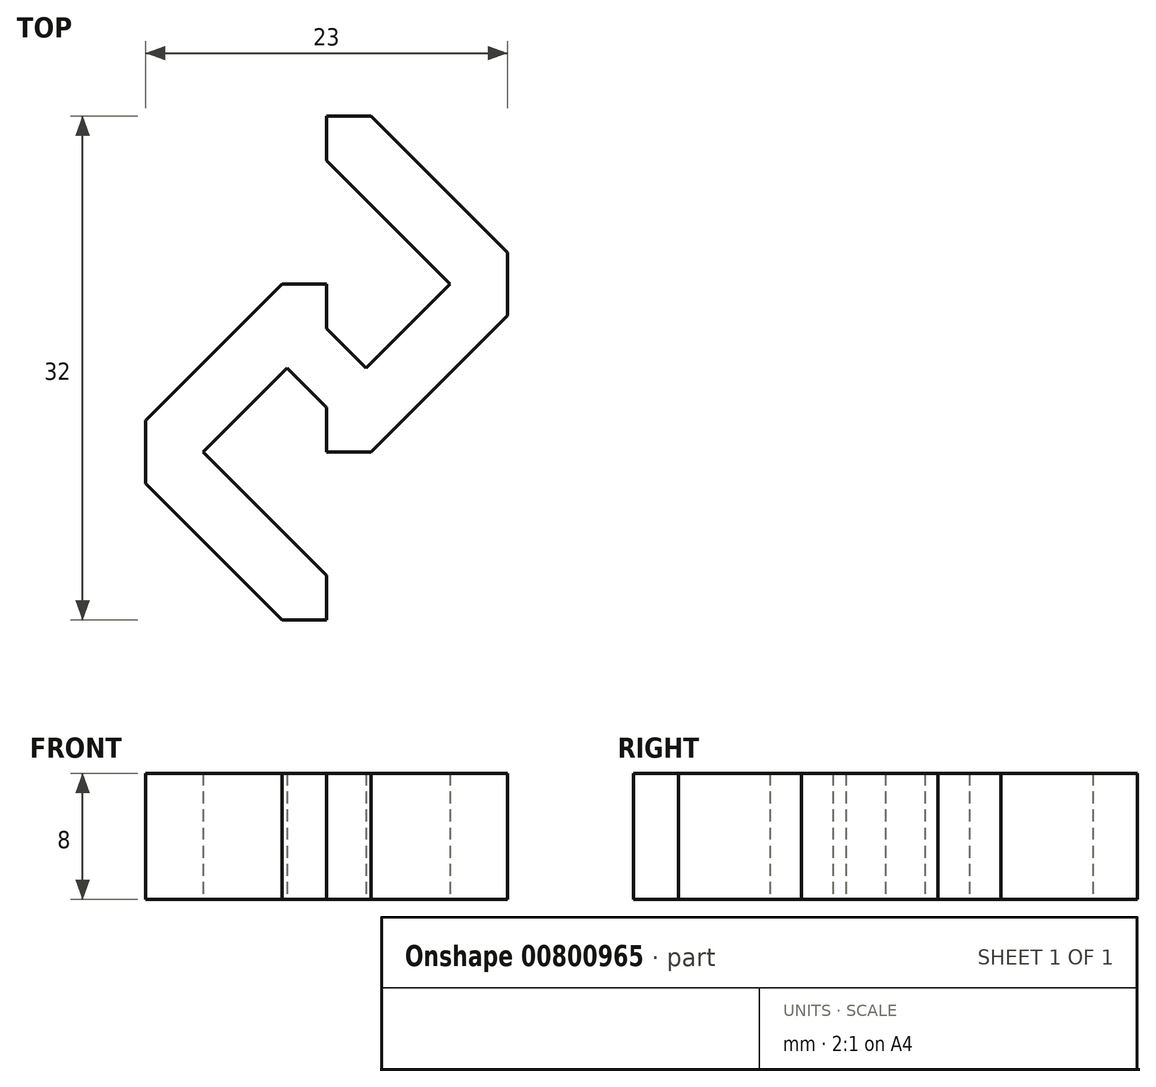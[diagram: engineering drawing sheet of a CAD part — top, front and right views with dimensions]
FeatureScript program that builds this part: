
annotation { "Feature Type Name" : "Feature", "Feature Type Description" : "" }
export const myFeature = defineFeature(function(context is Context, id is Id, definition is map)
    precondition{}
    {
        {
            var Q0;
            Q0=qCreatedBy(makeId("Top.planeOp"),FACE);
            var sketch = newSketch(context, id + "F0", { "sketchPlane" : qUnion([Q0])});
            skLineSegment(sketch, "E0", {"start": v(0, 0) * mm, "end": v(0, -2.83) * mm});
            skLineSegment(sketch, "E1", {"start": v(0, -2.83) * mm, "end": v(7.84, -10.67) * mm});
            skLineSegment(sketch, "E2", {"start": v(7.84, -10.67) * mm, "end": v(0, -18.5) * mm});
            skLineSegment(sketch, "E3", {"start": v(0, 0) * mm, "end": v(2.83, 0) * mm});
            skLineSegment(sketch, "E4", {"start": v(2.83, 0) * mm, "end": v(11.5, -8.67) * mm});
            skLineSegment(sketch, "E5", {"start": v(11.5, -8.67) * mm, "end": v(11.5, -12.67) * mm});
            skLineSegment(sketch, "E6", {"start": v(11.5, -12.67) * mm, "end": v(2.83, -21.33) * mm});
            skLineSegment(sketch, "E7", {"start": v(2.83, -21.33) * mm, "end": v(0, -21.33) * mm});
            skLineSegment(sketch, "E8", {"start": v(0, -21.33) * mm, "end": v(0, -18.5) * mm});
            skLineSegment(sketch, "E9", {"start": v(0, -13.5) * mm, "end": v(0, -10.67) * mm});
            skLineSegment(sketch, "E10", {"start": v(0, -10.67) * mm, "end": v(-2.83, -10.67) * mm});
            skLineSegment(sketch, "E11", {"start": v(-2.83, -10.67) * mm, "end": v(-11.5, -19.33) * mm});
            skLineSegment(sketch, "E12", {"start": v(-11.5, -19.33) * mm, "end": v(-11.5, -23.33) * mm});
            skLineSegment(sketch, "E13", {"start": v(-11.5, -23.33) * mm, "end": v(-2.83, -32) * mm});
            skLineSegment(sketch, "E14", {"start": v(-2.83, -32) * mm, "end": v(0, -32) * mm});
            skLineSegment(sketch, "E15", {"start": v(0, -32) * mm, "end": v(0, -29.17) * mm});
            skLineSegment(sketch, "E16", {"start": v(0, -29.17) * mm, "end": v(-7.84, -21.33) * mm});
            skLineSegment(sketch, "E17", {"start": v(-7.84, -21.33) * mm, "end": v(0, -13.5) * mm});
            skLineSegment(sketch, "E18", {"start": v(0, -13.5) * mm, "end": v(2.5, -16) * mm});
            skLineSegment(sketch, "E19", {"start": v(2.5, -16) * mm, "end": v(0, -18.5) * mm});
            skLineSegment(sketch, "E20", {"start": v(0, -18.5) * mm, "end": v(-2.5, -16) * mm});
            skLineSegment(sketch, "E21", {"start": v(-2.5, -16) * mm, "end": v(0, -13.5) * mm});
            skSolve(sketch);
        }
        {
            var Q0;
            Q0 = qSketchRegion(id + "F0", true);
            extrude(context, id + "F1", {"entities" : qUnion([Q0]), "depth" : 8 * mm, "offsetDistance" : 25 * mm});
        }
    });
